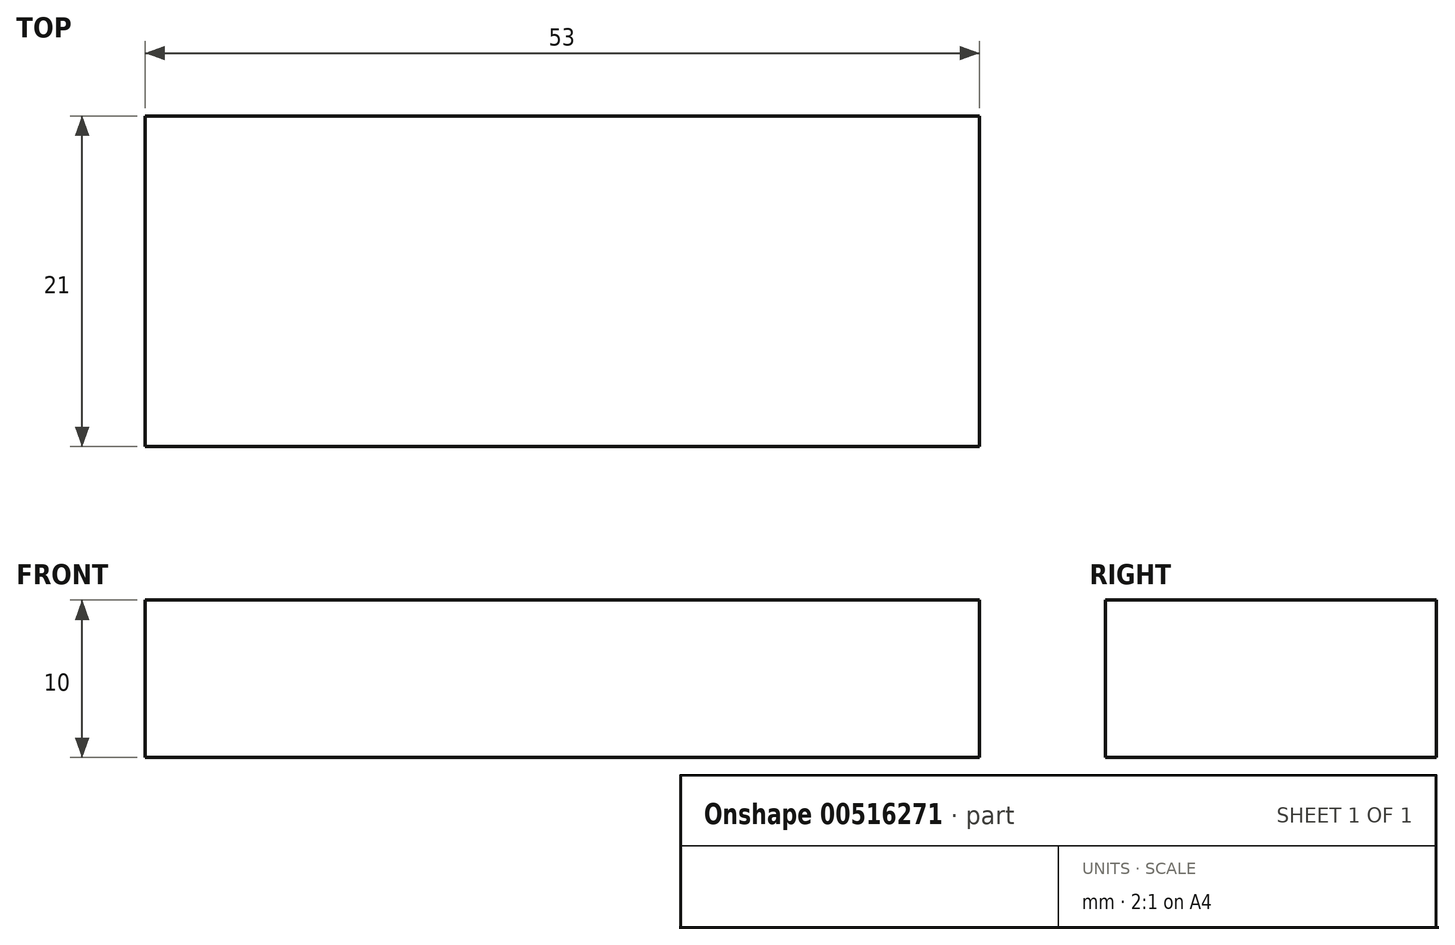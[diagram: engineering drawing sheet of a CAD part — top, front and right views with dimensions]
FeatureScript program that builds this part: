
annotation { "Feature Type Name" : "Feature", "Feature Type Description" : "" }
export const myFeature = defineFeature(function(context is Context, id is Id, definition is map)
    precondition{}
    {
        {
            var Q0;
            Q0=qCreatedBy(makeId("Top.planeOp"),FACE);
            var sketch = newSketch(context, id + "F0", { "sketchPlane" : qUnion([Q0])});
            skLineSegment(sketch, "E0.bottom", {"start": v(26.5, 10.5) * mm, "end": v(-26.5, 10.5) * mm});
            skLineSegment(sketch, "E0.top", {"start": v(26.5, -10.5) * mm, "end": v(-26.5, -10.5) * mm});
            skLineSegment(sketch, "E0.left", {"start": v(26.5, 10.5) * mm, "end": v(26.5, -10.5) * mm});
            skLineSegment(sketch, "E0.right", {"start": v(-26.5, 10.5) * mm, "end": v(-26.5, -10.5) * mm});
            skPoint(sketch, "E0.middle", {"position": v(0, 0) * mm});
            skSolve(sketch);
        }
        {
            var Q0;
            Q0=makeQuery(id+"F0.imprint","IMPRINT",FACE,{"disambiguationData":[TD([[makeQuery(id+"F0.imprint","IMPRINT",EDGE,{"derivedFrom":sQuery(id+"F0.wireOp",EDGE,"E0.bottom")}),1.0]])]});
            extrude(context, id + "F1", {"entities" : qUnion([Q0]), "depth" : 10 * mm});
        }
    });
